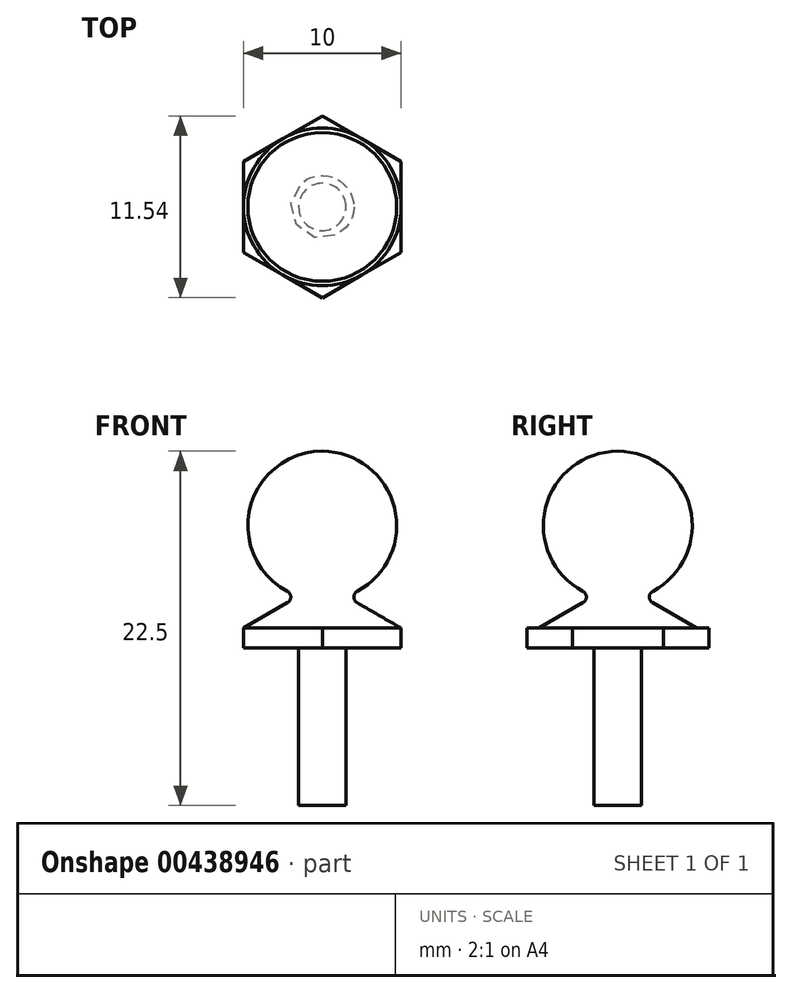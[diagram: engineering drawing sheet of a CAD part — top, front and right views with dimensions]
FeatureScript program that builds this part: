
annotation { "Feature Type Name" : "Feature", "Feature Type Description" : "" }
export const myFeature = defineFeature(function(context is Context, id is Id, definition is map)
    precondition{}
    {
        {
            var Q0;
            Q0=qCreatedBy(makeId("Front.planeOp"),FACE);
            var sketch = newSketch(context, id + "F0", { "sketchPlane" : qUnion([Q0])});
            skLineSegment(sketch, "E0", {"start": v(0, 21.14) * mm, "end": v(0, -20.68) * mm, "construction": true});
            skArc(sketch, "E1", {"start": v(0, 12.5) * mm, "mid": v(-4.58, 8.92) * mm, "end": v(-2.22, 3.6) * mm});
            skArc(sketch, "E2", {"start": v(-2.2, 2.88) * mm, "mid": v(-2, 3.25) * mm, "end": v(-2.22, 3.6) * mm});
            skLineSegment(sketch, "E3", {"start": v(-2.2, 2.88) * mm, "end": v(-5, 1.27) * mm});
            skLineSegment(sketch, "E4", {"start": v(-5, 1.27) * mm, "end": v(-5, 0) * mm});
            skLineSegment(sketch, "E5", {"start": v(-5, 0) * mm, "end": v(-1.5, 0) * mm});
            skLineSegment(sketch, "E6", {"start": v(0, 0) * mm, "end": v(0, 12.5) * mm});
            skLineSegment(sketch, "E7.top", {"start": v(0, -10) * mm, "end": v(-1.5, -10) * mm});
            skLineSegment(sketch, "E7.left", {"start": v(0, 0) * mm, "end": v(0, -10) * mm});
            skLineSegment(sketch, "E7.right", {"start": v(-1.5, 0) * mm, "end": v(-1.5, -10) * mm});
            skSolve(sketch);
        }
        {
            var Q0;
            Q0 = qSketchRegion(id + "F0", true);
            var Q1;
            Q1=sQuery(id+"F0.wireOp",EDGE,"E0");
            revolve(context, id + "F1", {"entities" : qUnion([Q0]), "axis" : qUnion([Q1]), "revolveType" : RevolveType.FULL});
        }
        {
            var Q0;
            Q0=qCreatedBy(makeId("Top.planeOp"),FACE);
            var sketch = newSketch(context, id + "F2", { "sketchPlane" : qUnion([Q0])});
            skCircle(sketch, "E8.cCircle", {"center": v(0, 0) * mm, "radius": 5 * mm, "construction": true});
            skLineSegment(sketch, "E8.0", {"start": v(5, 2.89) * mm, "end": v(5, -2.89) * mm});
            skLineSegment(sketch, "E8.1", {"start": v(5, -2.89) * mm, "end": v(0, -5.77) * mm});
            skLineSegment(sketch, "E8.2", {"start": v(0, -5.77) * mm, "end": v(-5, -2.89) * mm});
            skLineSegment(sketch, "E8.3", {"start": v(-5, -2.89) * mm, "end": v(-5, 2.89) * mm});
            skLineSegment(sketch, "E8.4", {"start": v(-5, 2.89) * mm, "end": v(0, 5.77) * mm});
            skLineSegment(sketch, "E8.5", {"start": v(0, 5.77) * mm, "end": v(5, 2.89) * mm});
            skPoint(sketch, "E8.0.midPoint", {"position": v(5, 0) * mm});
            skSolve(sketch);
        }
        {
            var Q0;
            Q0 = qSketchRegion(id + "F2", true);
            extrude(context, id + "F3", {"entities" : qUnion([Q0]), "operationType" : NewBodyOperationType.ADD, "depth" : 1.27 * mm});
        }
    });
